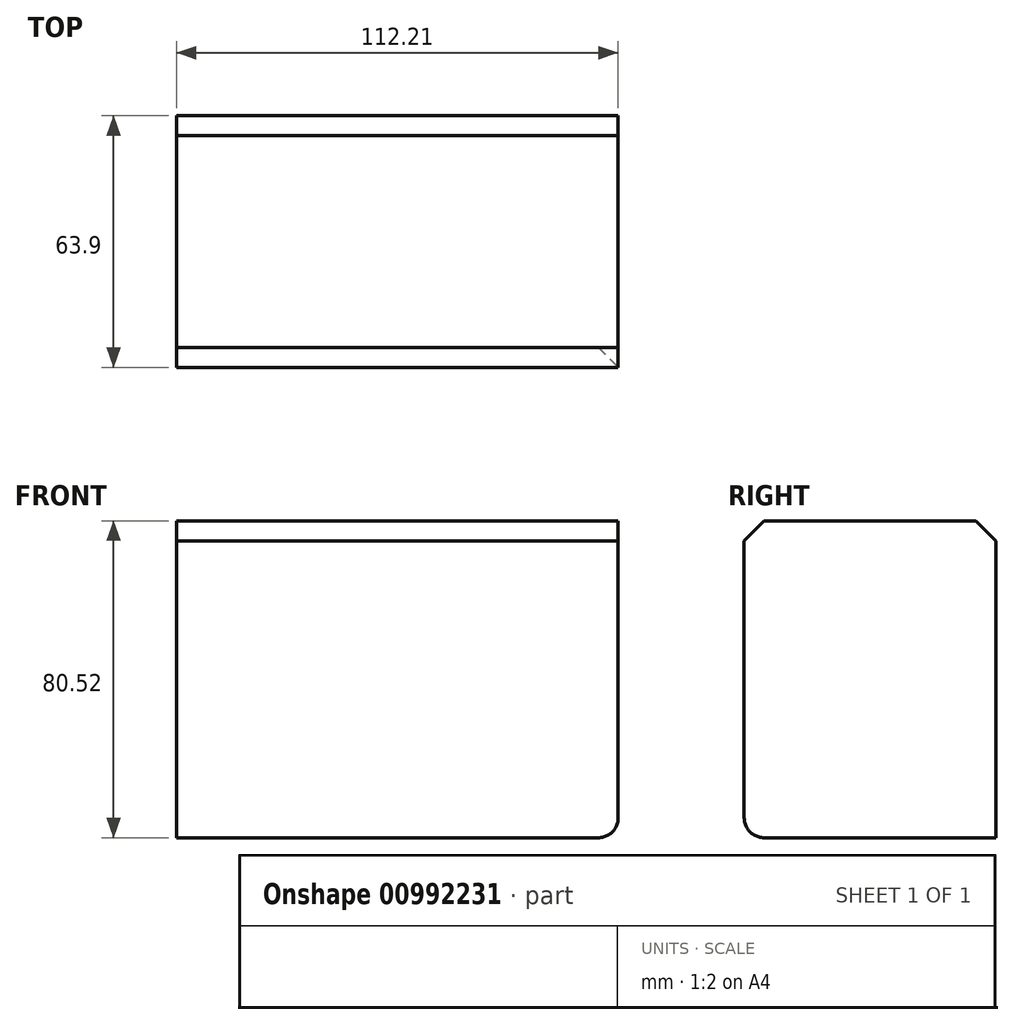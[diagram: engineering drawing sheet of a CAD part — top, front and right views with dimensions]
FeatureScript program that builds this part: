
annotation { "Feature Type Name" : "Feature", "Feature Type Description" : "" }
export const myFeature = defineFeature(function(context is Context, id is Id, definition is map)
    precondition{}
    {
        {
            var Q0;
            Q0=qCreatedBy(makeId("Top.planeOp"),FACE);
            var sketch = newSketch(context, id + "F0", { "sketchPlane" : qUnion([Q0])});
            skLineSegment(sketch, "E0.bottom", {"start": v(-54.37, -20.74) * mm, "end": v(57.84, -20.74) * mm});
            skLineSegment(sketch, "E0.top", {"start": v(-54.37, 43.16) * mm, "end": v(57.84, 43.16) * mm});
            skLineSegment(sketch, "E0.left", {"start": v(-54.37, -20.74) * mm, "end": v(-54.37, 43.16) * mm});
            skLineSegment(sketch, "E0.right", {"start": v(57.84, -20.74) * mm, "end": v(57.84, 43.16) * mm});
            skSolve(sketch);
        }
        {
            var Q0;
            Q0=makeQuery(id+"F0.imprint","IMPRINT",FACE,{"disambiguationData":[TD([[makeQuery(id+"F0.imprint","IMPRINT",EDGE,{"derivedFrom":sQuery(id+"F0.wireOp",EDGE,"E0.bottom")}),1.0]])]});
            extrude(context, id + "F1", {"entities" : qUnion([Q0]), "depth" : 80.52 * mm, "offsetDistance" : 25.4 * mm});
        }
        {
            var Q0;
            Q0=makeQuery(id+"F1.opExtrude","CAP_EDGE",EDGE,{"disambiguationData":[OSD([sQuery(id+"F0.wireOp",EDGE,"E0.bottom")])],"isStart":false});
            chamfer(context, id + "F2", {"entities" : qUnion([Q0]), "width" : 5.08 * mm, "tangentPropagation" : true});
        }
        {
            var Q0;
            Q0=makeQuery(id+"F1.opExtrude","CAP_EDGE",EDGE,{"disambiguationData":[OSD([sQuery(id+"F0.wireOp",EDGE,"E0.top")])],"isStart":false});
            chamfer(context, id + "F3", {"entities" : qUnion([Q0]), "width" : 5.08 * mm, "tangentPropagation" : true});
        }
        {
            var Q0;
            Q0=makeQuery(id+"F1.opExtrude","CAP_EDGE",EDGE,{"disambiguationData":[OSD([sQuery(id+"F0.wireOp",EDGE,"E0.bottom")])],"isStart":true});
            var Q1;
            Q1=makeQuery(id+"F1.opExtrude","CAP_EDGE",EDGE,{"disambiguationData":[OSD([sQuery(id+"F0.wireOp",EDGE,"E0.right")])],"isStart":true});
            fillet(context, id + "F4", {"entities" : qUnion([Q0, Q1]), "radius" : 5.08 * mm, "tangentPropagation" : true, "allowEdgeOverflow" : false});
        }
    });
